# Revit family: Domotics-DomesticRanges-GEWISS-CHORUS_POWER-SOCKET-OUTLET_DEU
name_source: partatom
category: Apparecchi elettrici
revit_build: Autodesk Revit 2016 (Build: 20161004_0715(x64)
units: mm (PartAtom-declared; Revit-internal decimal feet)

## family parameters
Condiviso = Sì
Host = Superficie
Mantenere orientamento annotazione = Sì
Punto di calcolo locali = Sì
Quota connettore circolare = Usa diametro
Taglio con vuoti quando caricato = Sì
Tipo di parte = Normale

## types (8) — shared parameters
Breaking capacity: = 1.25 In (100 position changes)
Carico apparente = 0 VA
Catalogue = DOMOTICS
Catalogue Range = CHORUS - DOMESTIC RANGE
Characteristics = With safety shields
Description: = 2P+E - 16A
Electrocod = 0131
For plug pins = Ã˜ 4.8 mm
Glow Wire Test = 850°C
IDF = 1e5c0e1f-8c6b-41bc-9da2-06778d33d87f
IDT = 310c0367-30fd-42b5-ab9c-fc234f86b9d5
Immagine tipo = GW14341.jpg
Insulation resistance = > 5 MOhm
N. poli = 1
No. Chorus modules = 2
No. Chorus modules: = 2
Produttore = GEWISS S.p.A.
Prolonged operation (no.of position changes) = 10.000 at In 250 V ac cosÃ˜=0,8
Prospetto di default = 1219 mm
Resistance at test voltage = 2000 V at 50 Hz for 1 minute
SEO = Socket outlet
Standard = German
Standard: = German
TXT ELETTRICO = 16
Technical sheet = https://www.gewiss.com
Terminal grip on cable traction = > 50 N
Terminal tightening capacity flexible cables (mm2) = min. 0,75 - max. 2x4
Terminal tightening capacity rigid cables (mm2) = min. 0,5 - max. 2x2,5
Thermo-pressure with ball = 125
Tipo_ = Chorus Prese Ger_GENERICO : GW14341 Presa 2M 2P+T 16A+ morsetti frontali standard Tedesco titanio
URL = https://www.gewiss.com
Version file RFA = 19.0
Volt = 230 V
Voltage = 250 V ac
Voltage: = 250 V ac

## per-type parameters (varying)
| type | Category | Colour | Description. | Descrizione | EAN code | Modello | Standard; | Type | Type: | Wiring terminals |
| GW14241 - Socket outlet 2M 2P+E 16A german st titanium | Socket-outlet | Titanium | Socket-outlet | SOCKET 2M 2P+E 16A GERMAN ST TITANIUM | 8011564266353 | GW14241 | IEC 60884-1; DIN VDE 0620-1; UNE 20315-1-1 |  |  | With screw |
| GW10251 - Socket outlet 2M 2P+E 16A de red | Socket-outlet | Red | Socket-outlet | S. OUT. 2M 2P+E 16A DE RED | 8011564264946 | GW10251 | IEC 60884-1; DIN VDE 0620-1 | For allocated lines | For allocated lines | With screw |
| GW12341 - Socket outlet 2M 2P+E 16a+terminal spa.st.black | Dual amperage socket-outlet | Black | Dual amperage socket-outlet | SOCK. 2M 2P+E 16A+TERMINAL SPA.ST.BLACK | 8011564280762 | GW12341 | IEC 60884-1; DIN VDE 0620-1; UNE 20315-1-1 | Front terminals |  | Screws with front tightening terminals |
| GW10241 - Socket outlet 2M 2P+E 16A de white | Socket-outlet | White | Socket-outlet | S. OUT. 2M 2P+E 16A DE WHITE | 8011564257955 | GW10241 | IEC 60884-1; DIN VDE 0620-1; UNE 20315-1-1 |  |  | With screw |
| GW10341 - Socket outlet 2M 2P+E 16A de front terminals white | Dual amperage socket-outlet | White | Dual amperage socket-outlet | S. OUT. 2M 2P+E 16A DE FRONT TERMINALS W | 8011564280755 | GW10341 | IEC 60884-1; DIN VDE 0620-1; UNE 20315-1-1 | Front terminals |  | Screws with front tightening terminals |
| GW10351 - Socket outlet 2M 2P+E 16A de front terminals red | Dual amperage socket-outlet | Red | Dual amperage socket-outlet | S. OUT. 2M 2P+E 16A DE FRONT TERMINALS R | 8011564280786 | GW10351 | IEC 60884-1; DIN VDE 0620-1; UNE 20315-1-1 | Front terminals |  | Screws with front tightening terminals |
| GW14341 - Socket outlet 2M 2P+E 16a+terminal spa.st.titanium | Dual amperage socket-outlet | Titanium | Dual amperage socket-outlet | SOCK. 2M 2P+E 16A+TERMINAL SPA.ST.TIT. | 8011564280779 | GW14341 | IEC 60884-1; DIN VDE 0620-1; UNE 20315-1-1 | Front terminals |  | Screws with front tightening terminals |
| GW12241 - Socket outlet 2M 2P+E 16A german st black | Socket-outlet | Black | Socket-outlet | SOCKET 2M 2P+E 16A GERMAN ST BLACK | 8011564266919 | GW12241 | IEC 60884-1; DIN VDE 0620-1; UNE 20315-1-1 |  |  | With screw |

note: source unit labels omitted for Thermo-pressure with ball — the stored unit's dimension contradicts the parameter name (converter mislabeling)

## geometry (parser evidence)
native form markers: Sweep x2
no freeform markers — native parametric forms only
